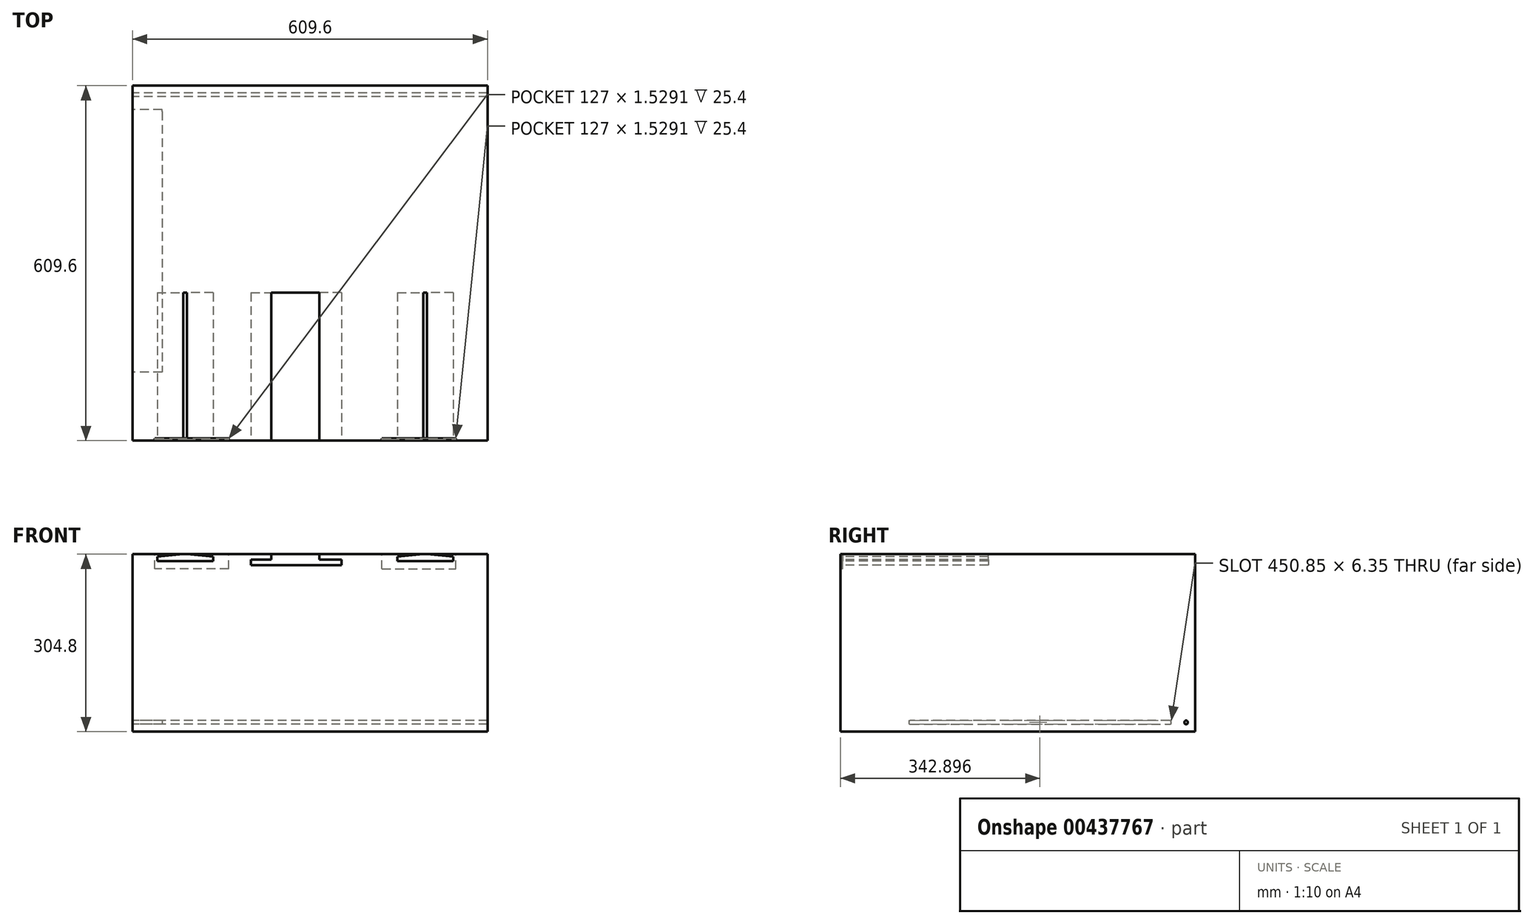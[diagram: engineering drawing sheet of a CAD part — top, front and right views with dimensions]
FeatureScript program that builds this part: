
annotation { "Feature Type Name" : "Feature", "Feature Type Description" : "" }
export const myFeature = defineFeature(function(context is Context, id is Id, definition is map)
    precondition{}
    {
        {
            var Q0;
            Q0=qCreatedBy(makeId("Top.planeOp"),FACE);
            var sketch = newSketch(context, id + "F0", { "sketchPlane" : qUnion([Q0])});
            skLineSegment(sketch, "E0.bottom", {"start": v(313, 345.57) * mm, "end": v(-296.6, 345.57) * mm});
            skLineSegment(sketch, "E0.top", {"start": v(313, -264.03) * mm, "end": v(-296.6, -264.03) * mm});
            skLineSegment(sketch, "E0.left", {"start": v(313, 345.57) * mm, "end": v(313, -264.03) * mm});
            skLineSegment(sketch, "E0.right", {"start": v(-296.6, 345.57) * mm, "end": v(-296.6, -264.03) * mm});
            skSolve(sketch);
        }
        {
            var Q0;
            Q0 = qSketchRegion(id + "F0", true);
            extrude(context, id + "F1", {"entities" : qUnion([Q0]), "depth" : 304.8 * mm});
        }
        {
            var Q0;
            Q0=makeQuery(id+"F1.opExtrude","SWEPT_FACE",FACE,{"disambiguationData":[OSD([sQuery(id+"F0.wireOp",EDGE,"E0.right")])]});
            var sketch = newSketch(context, id + "F2", { "sketchPlane" : qUnion([Q0])});
            skCircle(sketch, "E1", {"center": v(-329.7, 15.88) * mm, "radius": 3.18 * mm});
            skSolve(sketch);
        }
        {
            var Q0;
            Q0 = qSketchRegion(id + "F2", true);
            extrude(context, id + "F3", {"entities" : qUnion([Q0]), "operationType" : NewBodyOperationType.REMOVE, "oppositeDirection" : true, "depth" : 609.6 * mm});
        }
        {
            var Q0;
            Q0=makeQuery(id+"F1.opExtrude","SWEPT_FACE",FACE,{"disambiguationData":[OSD([sQuery(id+"F0.wireOp",EDGE,"E0.right")])]});
            var sketch = newSketch(context, id + "F4", { "sketchPlane" : qUnion([Q0])});
            skArc(sketch, "E2", {"start": v(-301.12, 19.05) * mm, "mid": v(-304.3, 15.87) * mm, "end": v(-301.12, 12.7) * mm});
            skArc(sketch, "E3", {"start": v(143.38, 12.7) * mm, "mid": v(146.56, 15.88) * mm, "end": v(143.38, 19.05) * mm});
            skLineSegment(sketch, "E4", {"start": v(-301.12, 19.05) * mm, "end": v(143.38, 19.05) * mm});
            skLineSegment(sketch, "E5", {"start": v(143.38, 12.7) * mm, "end": v(-301.12, 12.7) * mm});
            skSolve(sketch);
        }
        {
            var Q0;
            Q0 = qSketchRegion(id + "F4", true);
            extrude(context, id + "F5", {"entities" : qUnion([Q0]), "operationType" : NewBodyOperationType.REMOVE, "oppositeDirection" : true, "depth" : 50.8 * mm});
        }
        {
            var Q0;
            Q0=makeQuery(id+"F1.opExtrude","SWEPT_FACE",FACE,{"disambiguationData":[OSD([sQuery(id+"F0.wireOp",EDGE,"E0.top")])]});
            var sketch = newSketch(context, id + "F6", { "sketchPlane" : qUnion([Q0])});
            skLineSegment(sketch, "E6.bottom", {"start": v(209.28, 304.8) * mm, "end": v(202.88, 304.8) * mm});
            skLineSegment(sketch, "E6.top", {"start": v(254, 292.79) * mm, "end": v(158.15, 292.79) * mm});
            skLineSegment(sketch, "E6.left", {"start": v(254, 304.8) * mm, "end": v(254, 300.3) * mm});
            skLineSegment(sketch, "E7", {"start": v(254, 300.3) * mm, "end": v(209.28, 304.8) * mm});
            skLineSegment(sketch, "E8", {"start": v(158.15, 300.3) * mm, "end": v(202.88, 304.8) * mm});
            skLineSegment(sketch, "E9", {"start": v(158.15, 292.79) * mm, "end": v(158.15, 300.3) * mm});
            skLineSegment(sketch, "E10", {"start": v(254, 292.79) * mm, "end": v(254, 300.3) * mm});
            skPoint(sketch, "E11.orphan", {"position": v(158.15, 304.8) * mm});
            skLineSegment(sketch, "E12", {"start": v(202.88, 304.8) * mm, "end": v(209.28, 304.8) * mm});
            skLineSegment(sketch, "E13.MirrorCS", {"start": v(-158.15, 292.79) * mm, "end": v(-158.15, 300.3) * mm});
            skLineSegment(sketch, "E14.MirrorCS", {"start": v(-158.15, 300.3) * mm, "end": v(-202.88, 304.8) * mm});
            skLineSegment(sketch, "E15.MirrorCS", {"start": v(-254, 292.79) * mm, "end": v(-158.15, 292.79) * mm});
            skLineSegment(sketch, "E16.MirrorCS", {"start": v(-202.88, 304.8) * mm, "end": v(-209.28, 304.8) * mm});
            skLineSegment(sketch, "E17.MirrorCS", {"start": v(-254, 300.3) * mm, "end": v(-209.28, 304.8) * mm});
            skLineSegment(sketch, "E18.MirrorCS", {"start": v(-254, 292.79) * mm, "end": v(-254, 300.3) * mm});
            skLineSegment(sketch, "E19.bottom", {"start": v(24.29, 304.8) * mm, "end": v(-58.27, 304.8) * mm});
            skLineSegment(sketch, "E19.top", {"start": v(62.35, 285.75) * mm, "end": v(-93.12, 285.75) * mm});
            skLineSegment(sketch, "E19.left", {"start": v(62.35, 295.27) * mm, "end": v(62.35, 285.75) * mm});
            skLineSegment(sketch, "E19.right", {"start": v(-93.12, 295.27) * mm, "end": v(-93.12, 285.75) * mm});
            skLineSegment(sketch, "E20", {"start": v(-93.12, 295.27) * mm, "end": v(-58.27, 295.27) * mm});
            skLineSegment(sketch, "E21", {"start": v(-58.27, 295.27) * mm, "end": v(-58.27, 304.8) * mm});
            skLineSegment(sketch, "E22", {"start": v(-58.27, 304.8) * mm, "end": v(24.29, 304.8) * mm});
            skLineSegment(sketch, "E23", {"start": v(24.29, 304.8) * mm, "end": v(24.29, 295.27) * mm});
            skLineSegment(sketch, "E24", {"start": v(24.29, 295.27) * mm, "end": v(62.35, 295.27) * mm});
            skPoint(sketch, "E25.orphan", {"position": v(-93.12, 304.8) * mm});
            skPoint(sketch, "E26.orphan", {"position": v(62.35, 304.8) * mm});
            skSolve(sketch);
        }
        {
            var Q0;
            Q0 = qSketchRegion(id + "F6", true);
            extrude(context, id + "F7", {"entities" : qUnion([Q0]), "operationType" : NewBodyOperationType.REMOVE, "oppositeDirection" : true, "depth" : 254 * mm});
        }
        {
            var Q0;
            Q0=makeQuery(id+"F1.opExtrude","CAP_FACE",FACE,{"disambiguationData":[OSD([sQuery(id+"F0.wireOp",EDGE,"E0.bottom"),sQuery(id+"F0.wireOp",EDGE,"E0.top"),sQuery(id+"F0.wireOp",EDGE,"E0.left"),sQuery(id+"F0.wireOp",EDGE,"E0.right")])],"isStart":false});
            var sketch = newSketch(context, id + "F8", { "sketchPlane" : qUnion([Q0])});
            skLineSegment(sketch, "E27.top", {"start": v(-131.5, -261.65) * mm, "end": v(-258.5, -261.65) * mm});
            skLineSegment(sketch, "E28", {"start": v(-131.5, -260.12) * mm, "end": v(-258.5, -260.12) * mm});
            skLineSegment(sketch, "E29", {"start": v(-258.5, -260.12) * mm, "end": v(-258.5, -261.65) * mm});
            skLineSegment(sketch, "E30", {"start": v(-131.5, -260.12) * mm, "end": v(-131.5, -261.65) * mm});
            skLineSegment(sketch, "E31.MirrorCS", {"start": v(131.5, -260.12) * mm, "end": v(258.5, -260.12) * mm});
            skLineSegment(sketch, "E32.MirrorCS", {"start": v(131.5, -261.65) * mm, "end": v(258.5, -261.65) * mm});
            skLineSegment(sketch, "E33.MirrorCS", {"start": v(258.5, -260.12) * mm, "end": v(258.5, -261.65) * mm});
            skLineSegment(sketch, "E34.MirrorCS", {"start": v(131.5, -260.12) * mm, "end": v(131.5, -261.65) * mm});
            skSolve(sketch);
        }
        {
            var Q0;
            Q0 = qSketchRegion(id + "F8", true);
            extrude(context, id + "F9", {"entities" : qUnion([Q0]), "operationType" : NewBodyOperationType.REMOVE, "oppositeDirection" : true, "depth" : 25.4 * mm});
        }
    });
